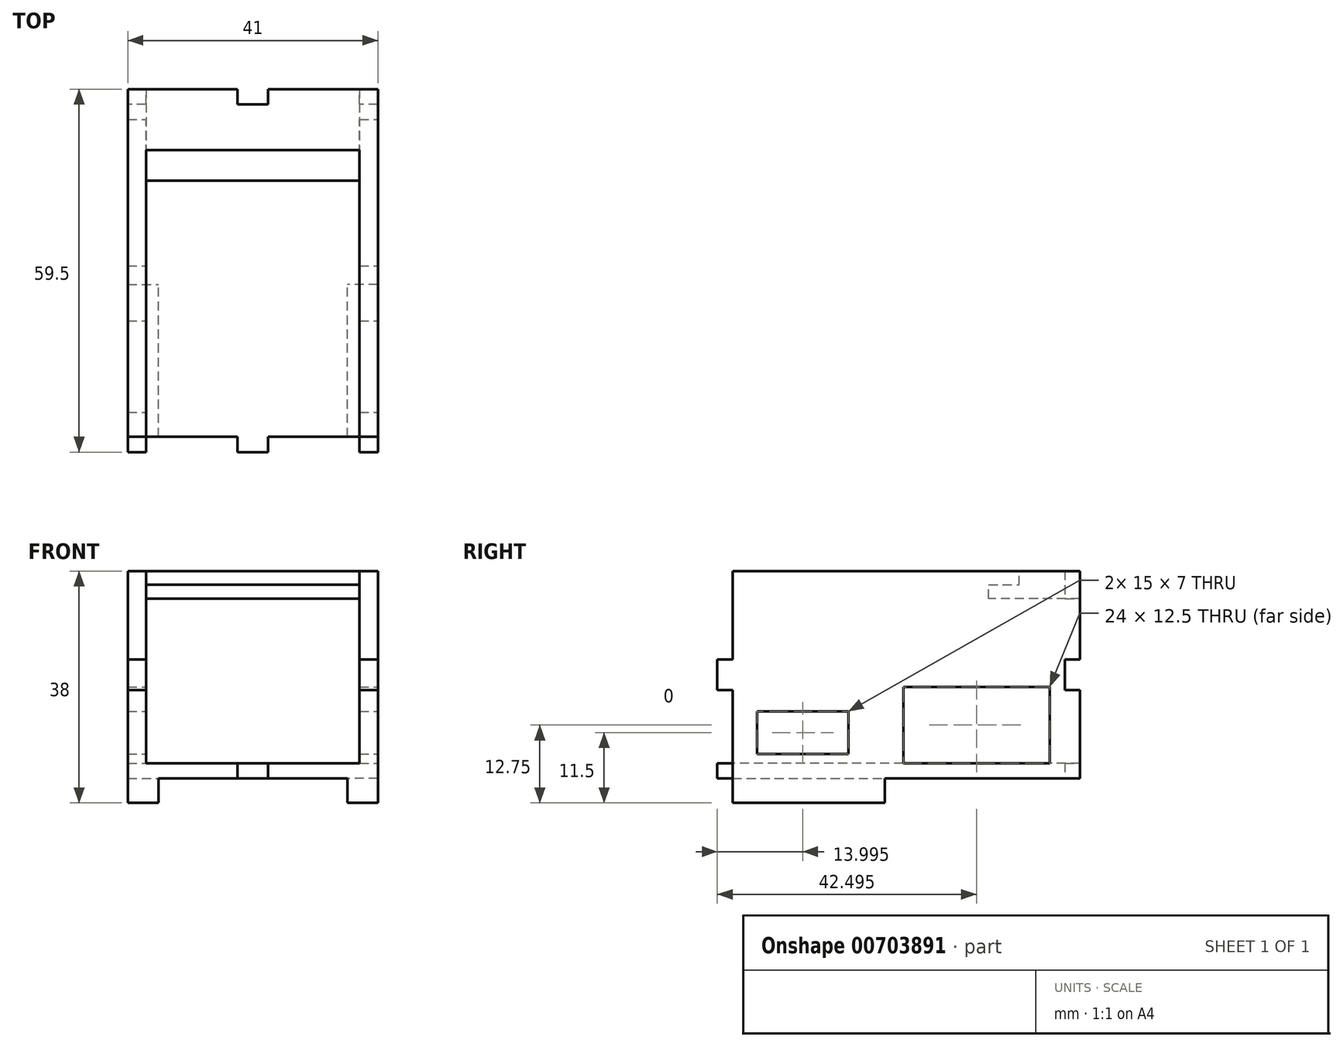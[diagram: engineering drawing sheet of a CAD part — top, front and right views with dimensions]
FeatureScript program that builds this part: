
annotation { "Feature Type Name" : "Feature", "Feature Type Description" : "" }
export const myFeature = defineFeature(function(context is Context, id is Id, definition is map)
    precondition{}
    {
        {
            var Q0;
            Q0=qCreatedBy(makeId("Top.planeOp"),FACE);
            var sketch = newSketch(context, id + "F0", { "sketchPlane" : qUnion([Q0])});
            skLineSegment(sketch, "E0.bottom", {"start": v(-20.97, 15.69) * mm, "end": v(20.03, 15.69) * mm});
            skLineSegment(sketch, "E0.top", {"start": v(-20.97, -41.31) * mm, "end": v(20.03, -41.31) * mm});
            skLineSegment(sketch, "E0.left", {"start": v(-20.97, 15.69) * mm, "end": v(-20.97, -41.31) * mm});
            skLineSegment(sketch, "E0.right", {"start": v(20.03, 15.69) * mm, "end": v(20.03, -41.31) * mm});
            skSolve(sketch);
        }
        {
            var Q0;
            Q0=makeQuery(id+"F0.imprint","IMPRINT",FACE,{"disambiguationData":[TD([[makeQuery(id+"F0.imprint","IMPRINT",EDGE,{"derivedFrom":sQuery(id+"F0.wireOp",EDGE,"E0.bottom")}),-1.0]])]});
            extrude(context, id + "F1", {"entities" : qUnion([Q0]), "depth" : 34 * mm, "offsetDistance" : 25 * mm});
        }
        {
            var Q0;
            Q0=makeQuery(id+"F1.opExtrude","SWEPT_FACE",FACE,{"disambiguationData":[OSD([sQuery(id+"F0.wireOp",EDGE,"E0.top")])]});
            var sketch = newSketch(context, id + "F2", { "sketchPlane" : qUnion([Q0])});
            skLineSegment(sketch, "E1.bottom", {"start": v(-17.97, 31.5) * mm, "end": v(17.03, 31.5) * mm});
            skLineSegment(sketch, "E1.top", {"start": v(-17.97, 2.5) * mm, "end": v(17.03, 2.5) * mm});
            skLineSegment(sketch, "E1.left", {"start": v(-17.97, 31.5) * mm, "end": v(-17.97, 2.5) * mm});
            skLineSegment(sketch, "E1.right", {"start": v(17.03, 31.5) * mm, "end": v(17.03, 2.5) * mm});
            skSolve(sketch);
        }
        {
            var Q0;
            Q0=makeQuery(id+"F2.imprint","IMPRINT",FACE,{"disambiguationData":[TD([[makeQuery(id+"F2.imprint","IMPRINT",EDGE,{"derivedFrom":sQuery(id+"F2.wireOp",EDGE,"E1.bottom")}),-1.0]])]});
            extrude(context, id + "F3", {"entities" : qUnion([Q0]), "operationType" : NewBodyOperationType.REMOVE, "endBound" : BoundingType.UP_TO_NEXT, "oppositeDirection" : true, "depth" : 25 * mm, "offsetDistance" : 25 * mm});
        }
        {
            var Q0;
            Q0=makeQuery(id+"F1.opExtrude","SWEPT_FACE",FACE,{"disambiguationData":[OSD([sQuery(id+"F0.wireOp",EDGE,"E0.bottom")])]});
            var sketch = newSketch(context, id + "F4", { "sketchPlane" : qUnion([Q0])});
            skLineSegment(sketch, "E2.bottom", {"start": v(-2.03, 34) * mm, "end": v(2.97, 34) * mm});
            skLineSegment(sketch, "E2.top", {"start": v(-2.03, 31.5) * mm, "end": v(2.97, 31.5) * mm});
            skLineSegment(sketch, "E2.left", {"start": v(-2.03, 34) * mm, "end": v(-2.03, 31.5) * mm});
            skLineSegment(sketch, "E2.right", {"start": v(2.97, 34) * mm, "end": v(2.97, 31.5) * mm});
            skLineSegment(sketch, "E3.bottom", {"start": v(-2.03, 2.5) * mm, "end": v(2.97, 2.5) * mm});
            skLineSegment(sketch, "E3.top", {"start": v(-2.03, 0) * mm, "end": v(2.97, 0) * mm});
            skLineSegment(sketch, "E3.left", {"start": v(-2.03, 2.5) * mm, "end": v(-2.03, 0) * mm});
            skLineSegment(sketch, "E3.right", {"start": v(2.97, 2.5) * mm, "end": v(2.97, 0) * mm});
            skLineSegment(sketch, "E4.bottom", {"start": v(-20.03, 19.5) * mm, "end": v(-17.03, 19.5) * mm});
            skLineSegment(sketch, "E4.top", {"start": v(-20.03, 14.5) * mm, "end": v(-17.03, 14.5) * mm});
            skLineSegment(sketch, "E4.left", {"start": v(-20.03, 19.5) * mm, "end": v(-20.03, 14.5) * mm});
            skLineSegment(sketch, "E4.right", {"start": v(-17.03, 19.5) * mm, "end": v(-17.03, 14.5) * mm});
            skLineSegment(sketch, "E5.bottom", {"start": v(17.97, 19.5) * mm, "end": v(20.97, 19.5) * mm});
            skLineSegment(sketch, "E5.top", {"start": v(17.97, 14.5) * mm, "end": v(20.97, 14.5) * mm});
            skLineSegment(sketch, "E5.left", {"start": v(17.97, 19.5) * mm, "end": v(17.97, 14.5) * mm});
            skLineSegment(sketch, "E5.right", {"start": v(20.97, 19.5) * mm, "end": v(20.97, 14.5) * mm});
            skSolve(sketch);
        }
        {
            var Q0;
            Q0=makeQuery(id+"F4.imprint","IMPRINT",FACE,{"disambiguationData":[TD([[makeQuery(id+"F4.imprint","IMPRINT",EDGE,{"derivedFrom":sQuery(id+"F4.wireOp",EDGE,"E4.bottom")}),-1.0]])]});
            var Q1;
            Q1=makeQuery(id+"F4.imprint","IMPRINT",FACE,{"disambiguationData":[TD([[makeQuery(id+"F4.imprint","IMPRINT",EDGE,{"derivedFrom":sQuery(id+"F4.wireOp",EDGE,"E2.bottom")}),1.0]])]});
            var Q2;
            Q2=makeQuery(id+"F4.imprint","IMPRINT",FACE,{"disambiguationData":[TD([[makeQuery(id+"F4.imprint","IMPRINT",EDGE,{"derivedFrom":sQuery(id+"F4.wireOp",EDGE,"E5.bottom")}),-1.0]])]});
            var Q3;
            Q3=makeQuery(id+"F4.imprint","IMPRINT",FACE,{"disambiguationData":[TD([[makeQuery(id+"F4.imprint","IMPRINT",EDGE,{"derivedFrom":sQuery(id+"F4.wireOp",EDGE,"E3.bottom")}),1.0]])]});
            extrude(context, id + "F5", {"entities" : qUnion([Q0, Q1, Q2, Q3]), "operationType" : NewBodyOperationType.REMOVE, "oppositeDirection" : true, "depth" : 2.5 * mm, "offsetDistance" : 25 * mm});
        }
        {
            var Q0;
            Q0=makeQuery(id+"F1.opExtrude","SWEPT_FACE",FACE,{"disambiguationData":[OSD([sQuery(id+"F0.wireOp",EDGE,"E0.top")])]});
            var sketch = newSketch(context, id + "F6", { "sketchPlane" : qUnion([Q0])});
            skLineSegment(sketch, "E6.bottom", {"start": v(-17.97, 31.5) * mm, "end": v(17.03, 31.5) * mm});
            skLineSegment(sketch, "E6.top", {"start": v(-17.97, 34) * mm, "end": v(17.03, 34) * mm});
            skLineSegment(sketch, "E6.left", {"start": v(-17.97, 31.5) * mm, "end": v(-17.97, 34) * mm});
            skLineSegment(sketch, "E6.right", {"start": v(17.03, 31.5) * mm, "end": v(17.03, 34) * mm});
            skSolve(sketch);
        }
        {
            var Q0;
            Q0=makeQuery(id+"F6.imprint","IMPRINT",FACE,{"disambiguationData":[TD([[makeQuery(id+"F6.imprint","IMPRINT",EDGE,{"derivedFrom":sQuery(id+"F6.wireOp",EDGE,"E6.bottom")}),1.0]])]});
            extrude(context, id + "F7", {"entities" : qUnion([Q0]), "operationType" : NewBodyOperationType.REMOVE, "oppositeDirection" : true, "depth" : 47 * mm, "offsetDistance" : 25 * mm});
        }
        {
            var Q0;
            Q0=makeQuery(id+"F1.opExtrude","SWEPT_FACE",FACE,{"disambiguationData":[OSD([sQuery(id+"F0.wireOp",EDGE,"E0.right")])]});
            var sketch = newSketch(context, id + "F8", { "sketchPlane" : qUnion([Q0])});
            skLineSegment(sketch, "E7.bottom", {"start": v(10.69, 2.5) * mm, "end": v(-13.31, 2.5) * mm});
            skLineSegment(sketch, "E7.top", {"start": v(10.69, 15) * mm, "end": v(-13.31, 15) * mm});
            skLineSegment(sketch, "E7.left", {"start": v(10.69, 2.5) * mm, "end": v(10.69, 15) * mm});
            skLineSegment(sketch, "E7.right", {"start": v(-13.31, 2.5) * mm, "end": v(-13.31, 15) * mm});
            skSolve(sketch);
        }
        {
            var Q0;
            Q0=makeQuery(id+"F8.imprint","IMPRINT",FACE,{"disambiguationData":[TD([[makeQuery(id+"F8.imprint","IMPRINT",EDGE,{"derivedFrom":sQuery(id+"F8.wireOp",EDGE,"E7.bottom")}),-1.0]])]});
            extrude(context, id + "F9", {"entities" : qUnion([Q0]), "operationType" : NewBodyOperationType.REMOVE, "endBound" : BoundingType.THROUGH_ALL, "oppositeDirection" : true, "depth" : 25 * mm, "offsetDistance" : 25 * mm});
        }
        {
            var Q0;
            Q0=makeQuery(id+"F1.opExtrude","CAP_FACE",FACE,{"disambiguationData":[OSD([sQuery(id+"F0.wireOp",EDGE,"E0.bottom"),sQuery(id+"F0.wireOp",EDGE,"E0.top"),sQuery(id+"F0.wireOp",EDGE,"E0.left"),sQuery(id+"F0.wireOp",EDGE,"E0.right")])],"isStart":true});
            var sketch = newSketch(context, id + "F10", { "sketchPlane" : qUnion([Q0])});
            skLineSegment(sketch, "E8.bottom", {"start": v(20.03, 41.31) * mm, "end": v(15.03, 41.31) * mm});
            skLineSegment(sketch, "E8.top", {"start": v(20.03, 16.31) * mm, "end": v(15.03, 16.31) * mm});
            skLineSegment(sketch, "E8.left", {"start": v(20.03, 41.31) * mm, "end": v(20.03, 16.31) * mm});
            skLineSegment(sketch, "E8.right", {"start": v(15.03, 41.31) * mm, "end": v(15.03, 16.31) * mm});
            skLineSegment(sketch, "E9.bottom", {"start": v(-20.97, 41.31) * mm, "end": v(-15.97, 41.31) * mm});
            skLineSegment(sketch, "E9.top", {"start": v(-20.97, 16.31) * mm, "end": v(-15.97, 16.31) * mm});
            skLineSegment(sketch, "E9.left", {"start": v(-20.97, 41.31) * mm, "end": v(-20.97, 16.31) * mm});
            skLineSegment(sketch, "E9.right", {"start": v(-15.97, 41.31) * mm, "end": v(-15.97, 16.31) * mm});
            skSolve(sketch);
        }
        {
            var Q0;
            Q0=makeQuery(id+"F10.imprint","IMPRINT",FACE,{"disambiguationData":[TD([[makeQuery(id+"F10.imprint","IMPRINT",EDGE,{"derivedFrom":sQuery(id+"F10.wireOp",EDGE,"E8.bottom")}),-1.0]])]});
            var Q1;
            Q1=makeQuery(id+"F10.imprint","IMPRINT",FACE,{"disambiguationData":[TD([[makeQuery(id+"F10.imprint","IMPRINT",EDGE,{"derivedFrom":sQuery(id+"F10.wireOp",EDGE,"E9.bottom")}),-1.0]])]});
            extrude(context, id + "F11", {"entities" : qUnion([Q0, Q1]), "operationType" : NewBodyOperationType.ADD, "depth" : 4 * mm, "offsetDistance" : 25 * mm});
        }
        {
            var Q0;
            Q0=makeQuery(id+"F11.boolean.opBoolean","MERGE",FACE,{"derivedFrom":[makeQuery(id+"F1.opExtrude","SWEPT_FACE",FACE,{"disambiguationData":[OSD([sQuery(id+"F0.wireOp",EDGE,"E0.right")])]}),makeQuery(id+"F11.opExtrude","SWEPT_FACE",FACE,{"disambiguationData":[OSD([sQuery(id+"F10.wireOp",EDGE,"E8.left")])]})]});
            var sketch = newSketch(context, id + "F12", { "sketchPlane" : qUnion([Q0])});
            skLineSegment(sketch, "E10.bottom", {"start": v(-37.31, 11) * mm, "end": v(-22.31, 11) * mm});
            skLineSegment(sketch, "E10.top", {"start": v(-37.31, 4) * mm, "end": v(-22.31, 4) * mm});
            skLineSegment(sketch, "E10.left", {"start": v(-37.31, 11) * mm, "end": v(-37.31, 4) * mm});
            skLineSegment(sketch, "E10.right", {"start": v(-22.31, 11) * mm, "end": v(-22.31, 4) * mm});
            skSolve(sketch);
        }
        {
            var Q0;
            Q0=makeQuery(id+"F12.imprint","IMPRINT",FACE,{"disambiguationData":[TD([[makeQuery(id+"F12.imprint","IMPRINT",EDGE,{"derivedFrom":sQuery(id+"F12.wireOp",EDGE,"E10.bottom")}),-1.0]])]});
            extrude(context, id + "F13", {"entities" : qUnion([Q0]), "operationType" : NewBodyOperationType.REMOVE, "endBound" : BoundingType.THROUGH_ALL, "oppositeDirection" : true, "depth" : 25 * mm, "offsetDistance" : 25 * mm});
        }
        {
            var Q0;
            Q0=makeQuery(id+"F3.boolean.opBoolean","COPY",FACE,{"derivedFrom":makeQuery(id+"F3.opExtrude","SWEPT_FACE",FACE,{"disambiguationData":[OSD([sQuery(id+"F2.wireOp",EDGE,"E1.bottom")])]})});
            extrude(context, id + "F14", {"entities" : qUnion([Q0]), "operationType" : NewBodyOperationType.ADD, "depth" : 2 * mm, "offsetDistance" : 25 * mm});
        }
        {
            var Q0;
            {var subQ0=sQuery(id+"F6.wireOp",EDGE,"E6.bottom");Q0=makeQuery(id+"F14.boolean.opBoolean","MERGE",FACE,{"derivedFrom":[makeQuery(id+"F7.boolean.opBoolean","COPY",FACE,{"derivedFrom":makeQuery(id+"F7.opExtrude","CAP_FACE",FACE,{"disambiguationData":[OSD([subQ0,sQuery(id+"F6.wireOp",EDGE,"E6.top"),sQuery(id+"F6.wireOp",EDGE,"E6.left"),sQuery(id+"F6.wireOp",EDGE,"E6.right")])],"isStart":false})}),makeQuery(id+"F14.opExtrude","SWEPT_FACE",FACE,{"disambiguationData":[OSD([subQ0])]})]});}
            var sketch = newSketch(context, id + "F15", { "sketchPlane" : qUnion([Q0])});
            skLineSegment(sketch, "E11.bottom", {"start": v(-17.97, 29.5) * mm, "end": v(17.03, 29.5) * mm});
            skLineSegment(sketch, "E11.top", {"start": v(-17.97, 31.75) * mm, "end": v(17.03, 31.75) * mm});
            skLineSegment(sketch, "E11.left", {"start": v(-17.97, 29.5) * mm, "end": v(-17.97, 31.75) * mm});
            skLineSegment(sketch, "E11.right", {"start": v(17.03, 29.5) * mm, "end": v(17.03, 31.75) * mm});
            skSolve(sketch);
        }
        {
            var Q0;
            Q0=makeQuery(id+"F15.imprint","IMPRINT",FACE,{"disambiguationData":[TD([[makeQuery(id+"F15.imprint","IMPRINT",EDGE,{"derivedFrom":sQuery(id+"F15.wireOp",EDGE,"E11.bottom")}),1.0]])]});
            extrude(context, id + "F16", {"entities" : qUnion([Q0]), "operationType" : NewBodyOperationType.ADD, "depth" : 5 * mm, "offsetDistance" : 25 * mm});
        }
        {
            var Q0;
            Q0=makeQuery(id+"F11.boolean.opBoolean","MERGE",FACE,{"derivedFrom":[makeQuery(id+"F1.opExtrude","SWEPT_FACE",FACE,{"disambiguationData":[OSD([sQuery(id+"F0.wireOp",EDGE,"E0.top")])]}),makeQuery(id+"F11.opExtrude","SWEPT_FACE",FACE,{"disambiguationData":[OSD([sQuery(id+"F10.wireOp",EDGE,"E8.bottom")])]}),makeQuery(id+"F11.opExtrude","SWEPT_FACE",FACE,{"disambiguationData":[OSD([sQuery(id+"F10.wireOp",EDGE,"E9.bottom")])]})]});
            var sketch = newSketch(context, id + "F17", { "sketchPlane" : qUnion([Q0])});
            skLineSegment(sketch, "E12.bottom", {"start": v(-2.97, 2.5) * mm, "end": v(2.03, 2.5) * mm});
            skLineSegment(sketch, "E12.top", {"start": v(-2.97, 0) * mm, "end": v(2.03, 0) * mm});
            skLineSegment(sketch, "E12.left", {"start": v(-2.97, 2.5) * mm, "end": v(-2.97, 0) * mm});
            skLineSegment(sketch, "E12.right", {"start": v(2.03, 2.5) * mm, "end": v(2.03, 0) * mm});
            skLineSegment(sketch, "E13.bottom", {"start": v(-20.97, 19.5) * mm, "end": v(-17.97, 19.5) * mm});
            skLineSegment(sketch, "E13.top", {"start": v(-20.97, 14.5) * mm, "end": v(-17.97, 14.5) * mm});
            skLineSegment(sketch, "E13.left", {"start": v(-20.97, 19.5) * mm, "end": v(-20.97, 14.5) * mm});
            skLineSegment(sketch, "E13.right", {"start": v(-17.97, 19.5) * mm, "end": v(-17.97, 14.5) * mm});
            skLineSegment(sketch, "E14.bottom", {"start": v(17.03, 19.5) * mm, "end": v(20.03, 19.5) * mm});
            skLineSegment(sketch, "E14.top", {"start": v(17.03, 14.5) * mm, "end": v(20.03, 14.5) * mm});
            skLineSegment(sketch, "E14.left", {"start": v(17.03, 19.5) * mm, "end": v(17.03, 14.5) * mm});
            skLineSegment(sketch, "E14.right", {"start": v(20.03, 19.5) * mm, "end": v(20.03, 14.5) * mm});
            skSolve(sketch);
        }
        {
            var Q0;
            Q0=makeQuery(id+"F17.imprint","IMPRINT",FACE,{"disambiguationData":[TD([[makeQuery(id+"F17.imprint","IMPRINT",EDGE,{"derivedFrom":sQuery(id+"F17.wireOp",EDGE,"E14.bottom")}),-1.0]])]});
            var Q1;
            Q1=makeQuery(id+"F17.imprint","IMPRINT",FACE,{"disambiguationData":[TD([[makeQuery(id+"F17.imprint","IMPRINT",EDGE,{"derivedFrom":sQuery(id+"F17.wireOp",EDGE,"E13.bottom")}),-1.0]])]});
            var Q2;
            Q2=makeQuery(id+"F17.imprint","IMPRINT",FACE,{"disambiguationData":[TD([[makeQuery(id+"F17.imprint","IMPRINT",EDGE,{"derivedFrom":sQuery(id+"F17.wireOp",EDGE,"E12.bottom")}),-1.0]])]});
            extrude(context, id + "F18", {"entities" : qUnion([Q0, Q1, Q2]), "operationType" : NewBodyOperationType.ADD, "depth" : 2.5 * mm, "offsetDistance" : 25 * mm});
        }
    });
